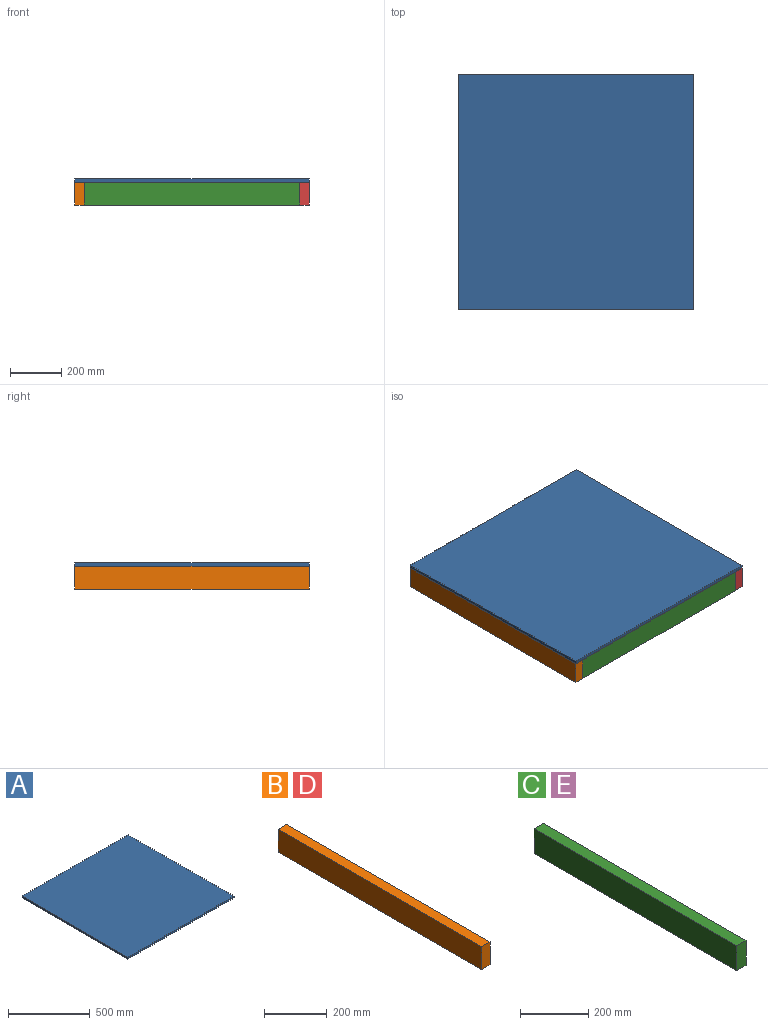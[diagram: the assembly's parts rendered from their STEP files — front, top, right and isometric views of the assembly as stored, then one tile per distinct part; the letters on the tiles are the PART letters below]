
ASSEMBLY  parts=5 mates=12
PART A: 6 faces, bbox 914.4x914.4x12.7 mm
  f0: plane 914.4x12.7mm, normal (1,0,0), area 11612.9mm2, adj f1,f3,f4,f5
  f1: plane 914.4x12.7mm, normal (0,1,0), area 11612.9mm2, adj f0,f2,f4,f5
  f2: plane 914.4x12.7mm, normal (-1,0,0), area 11612.9mm2, adj f1,f3,f4,f5
  f3: plane 914.4x12.7mm, normal (0,-1,0), area 11612.9mm2, adj f0,f2,f4,f5
  f4: plane 914.4x914.4mm, normal (0,0,-1), area 836127.4mm2, adj f0,f1,f2,f3
  f5: plane 914.4x914.4mm, normal (0,0,1), area 836127.4mm2, adj f0,f1,f2,f3
PART B: 6 faces, bbox 38.1x914.4x88.9 mm
  f0: plane 914.4x88.9mm, normal (1,0,0), area 81290.2mm2, adj f1,f3,f4,f5
  f1: plane 914.4x38.1mm, normal (0,0,1), area 34838.6mm2, adj f0,f2,f4,f5
  f2: plane 914.4x88.9mm, normal (-1,0,0), area 81290.2mm2, adj f1,f3,f4,f5
  f3: plane 914.4x38.1mm, normal (0,0,-1), area 34838.6mm2, adj f0,f2,f4,f5
  f4: plane 88.9x38.1mm, normal (0,-1,0), area 3387.1mm2, adj f0,f1,f2,f3
  f5: plane 88.9x38.1mm, normal (0,1,0), area 3387.1mm2, adj f0,f1,f2,f3
PART C: 6 faces, bbox 38.1x838.2x88.9 mm
  f0: plane 838.2x38.1mm, normal (0,0,-1), area 31935.4mm2, adj f1,f3,f4,f5
  f1: plane 838.2x88.9mm, normal (1,0,0), area 74516mm2, adj f0,f2,f4,f5
  f2: plane 838.2x38.1mm, normal (0,0,1), area 31935.4mm2, adj f1,f3,f4,f5
  f3: plane 838.2x88.9mm, normal (-1,0,0), area 74516mm2, adj f0,f2,f4,f5
  f4: plane 88.9x38.1mm, normal (0,-1,0), area 3387.1mm2, adj f0,f1,f2,f3
  f5: plane 88.9x38.1mm, normal (0,1,0), area 3387.1mm2, adj f0,f1,f2,f3
PART D: same geometry as B
PART E: same geometry as C
PLACE A t=(437.76,-2.17,3.43)mm
PLACE B t=(-0.39,455.03,-53.72)mm
PLACE C rot(axis=(0,0,-1),90deg) t=(856.86,-440.32,-53.72)mm
PLACE D t=(875.91,455.03,-53.72)mm
PLACE E rot(axis=(0,0,1),90deg) t=(18.66,435.98,-53.72)mm
MATE planar C.f4 <-> B.f0  axis (-1,0,0) through (18.66,-440.32,-53.72)mm
MATE planar D.f0 <-> A.f0  axis (1,0,0) through (894.96,-2.17,-53.72)mm
MATE planar B.f4 <-> A.f3  axis (0,-1,0) through (-0.39,-459.37,-53.72)mm
MATE planar A.f3 <-> D.f4  axis (0,-1,0) through (437.76,-459.37,-2.92)mm
MATE planar B.f2 <-> A.f2  axis (-1,0,0) through (-19.44,-2.17,-53.72)mm
MATE planar B.f1 <-> A.f4  axis (0,0,1) through (-0.39,-2.17,-9.27)mm
MATE planar D.f1 <-> A.f4  axis (0,0,1) through (875.91,-2.17,-9.27)mm
MATE planar E.f2 <-> A.f4  axis (0,0,1) through (437.76,435.98,-9.27)mm
MATE planar E.f5 <-> B.f0  axis (-1,0,0) through (18.66,435.98,-53.72)mm
MATE planar C.f2 <-> A.f4  axis (0,0,1) through (437.76,-440.32,-9.27)mm
MATE planar C.f1 <-> A.f3  axis (0,-1,0) through (437.76,-459.37,-53.72)mm
MATE planar E.f1 <-> A.f1  axis (0,1,0) through (437.76,455.03,-53.72)mm
